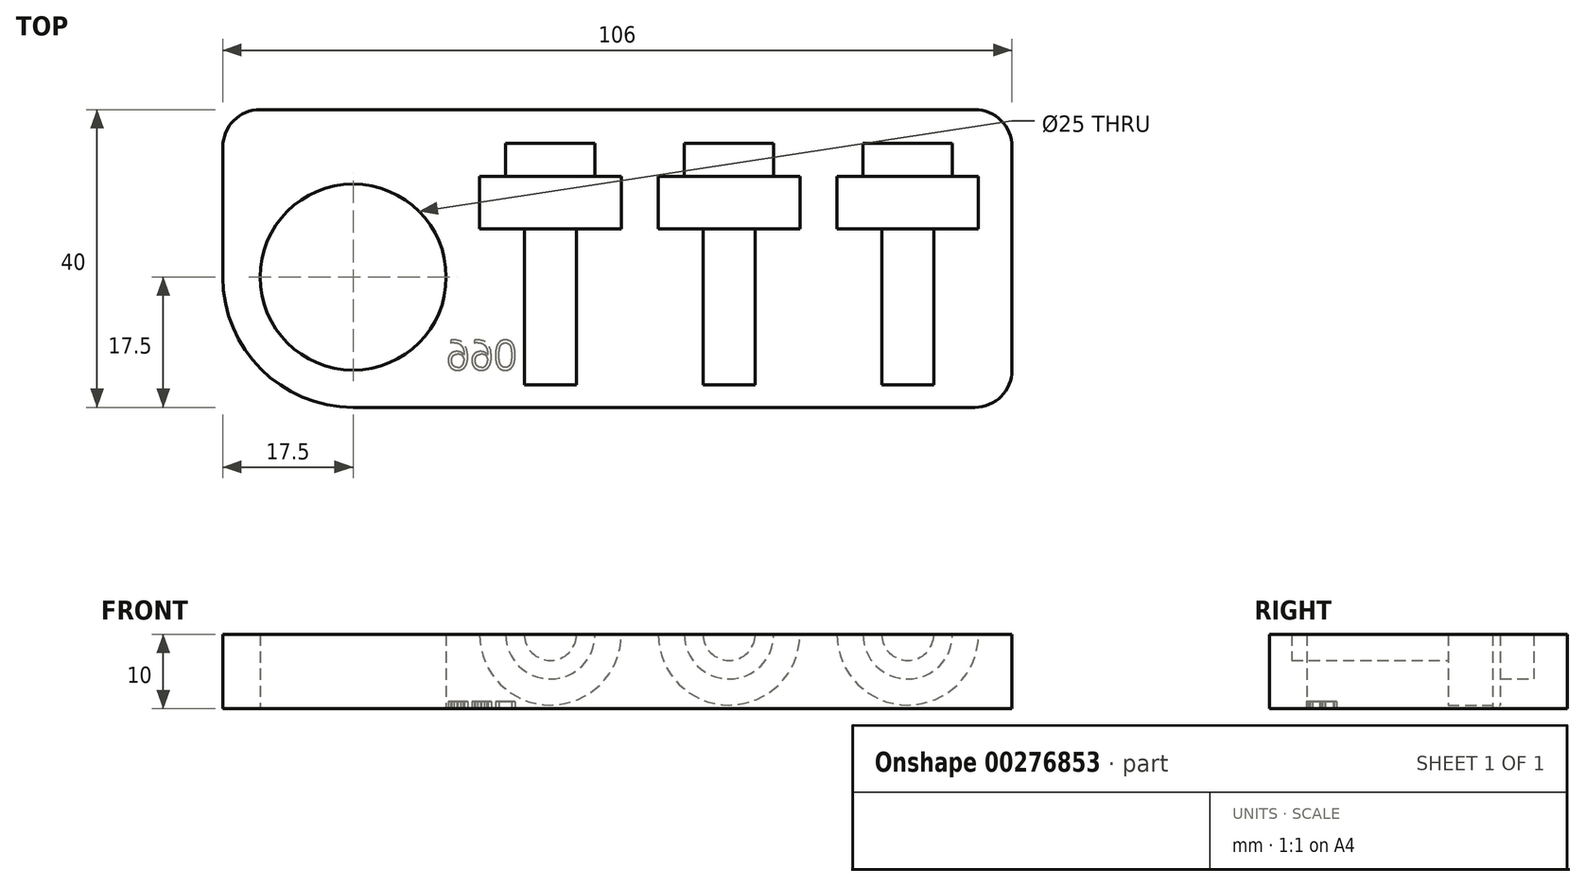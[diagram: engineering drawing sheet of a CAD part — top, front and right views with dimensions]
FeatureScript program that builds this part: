
annotation { "Feature Type Name" : "Feature", "Feature Type Description" : "" }
export const myFeature = defineFeature(function(context is Context, id is Id, definition is map)
    precondition{}
    {
        {
            var Q0;
            Q0=qCreatedBy(makeId("Top.planeOp"),FACE);
            var sketch = newSketch(context, id + "F0", { "sketchPlane" : qUnion([Q0])});
            skLineSegment(sketch, "E0.bottom", {"start": v(17.5, 0) * mm, "end": v(101, 0) * mm});
            skLineSegment(sketch, "E0.top", {"start": v(5, 40) * mm, "end": v(101, 40) * mm});
            skLineSegment(sketch, "E0.left", {"start": v(0, 17.5) * mm, "end": v(0, 35) * mm});
            skLineSegment(sketch, "E0.right", {"start": v(106, 5) * mm, "end": v(106, 35) * mm});
            skLineSegment(sketch, "E1.bottom", {"start": v(0, 0) * mm, "end": v(17.5, 0) * mm, "construction": true});
            skLineSegment(sketch, "E1.top", {"start": v(0, 17.5) * mm, "end": v(17.5, 17.5) * mm, "construction": true});
            skLineSegment(sketch, "E1.left", {"start": v(0, 0) * mm, "end": v(0, 17.5) * mm, "construction": true});
            skLineSegment(sketch, "E1.right", {"start": v(17.5, 0) * mm, "end": v(17.5, 17.5) * mm, "construction": true});
            skCircle(sketch, "E2", {"center": v(17.5, 17.5) * mm, "radius": 12.5 * mm});
            skPoint(sketch, "E3.visualSharp", {"position": v(0, 0) * mm});
            skArc(sketch, "E3.filletArc", {"start": v(0, 17.5) * mm, "mid": v(5.13, 5.13) * mm, "end": v(17.5, 0) * mm});
            skPoint(sketch, "E4.visualSharp", {"position": v(0, 40) * mm});
            skArc(sketch, "E4.filletArc", {"start": v(5, 40) * mm, "mid": v(1.46, 38.54) * mm, "end": v(0, 35) * mm});
            skPoint(sketch, "E5.visualSharp", {"position": v(106, 40) * mm});
            skArc(sketch, "E5.filletArc", {"start": v(106, 35) * mm, "mid": v(104.54, 38.54) * mm, "end": v(101, 40) * mm});
            skPoint(sketch, "E6.visualSharp", {"position": v(106, 0) * mm});
            skArc(sketch, "E6.filletArc", {"start": v(101, 0) * mm, "mid": v(104.54, 1.46) * mm, "end": v(106, 5) * mm});
            skSolve(sketch);
        }
        {
            var Q0;
            Q0=makeQuery(id+"F0.imprint","IMPRINT",FACE,{"disambiguationData":[TD([[makeQuery(id+"F0.imprint","IMPRINT",EDGE,{"derivedFrom":sQuery(id+"F0.wireOp",EDGE,"E0.bottom")}),1.0]])]});
            extrude(context, id + "F1", {"entities" : qUnion([Q0]), "depth" : 10 * mm});
        }
        {
            var Q0;
            Q0=makeQuery(id+"F1.opExtrude","CAP_FACE",FACE,{"disambiguationData":[OSD([sQuery(id+"F0.wireOp",EDGE,"E0.bottom"),sQuery(id+"F0.wireOp",EDGE,"E0.top"),sQuery(id+"F0.wireOp",EDGE,"E0.right"),sQuery(id+"F0.wireOp",EDGE,"E2"),sQuery(id+"F0.wireOp",EDGE,"E3.filletArc"),sQuery(id+"F0.wireOp",EDGE,"E4.filletArc"),sQuery(id+"F0.wireOp",EDGE,"E5.filletArc"),sQuery(id+"F0.wireOp",EDGE,"E6.filletArc")])],"isStart":false});
            var sketch = newSketch(context, id + "F2", { "sketchPlane" : qUnion([Q0])});
            skLineSegment(sketch, "E7.bottom", {"start": v(0, 0) * mm, "end": v(44, 0) * mm, "construction": true});
            skLineSegment(sketch, "E7.top", {"start": v(0, 3) * mm, "end": v(44, 3) * mm, "construction": true});
            skLineSegment(sketch, "E7.left", {"start": v(0, 0) * mm, "end": v(0, 3) * mm, "construction": true});
            skLineSegment(sketch, "E7.right", {"start": v(44, 0) * mm, "end": v(44, 3) * mm, "construction": true});
            skLineSegment(sketch, "E8", {"start": v(44, 3) * mm, "end": v(68, 3) * mm, "construction": true});
            skLineSegment(sketch, "E9", {"start": v(68, 3) * mm, "end": v(92, 3) * mm, "construction": true});
            skLineSegment(sketch, "E10", {"start": v(92, 3) * mm, "end": v(116, 3) * mm, "construction": true});
            skLineSegment(sketch, "E11.bottom", {"start": v(44, 3) * mm, "end": v(47.5, 3) * mm});
            skLineSegment(sketch, "E11.left", {"start": v(44, 3) * mm, "end": v(44, 24) * mm});
            skLineSegment(sketch, "E11.right", {"start": v(47.5, 3) * mm, "end": v(47.5, 24) * mm});
            skLineSegment(sketch, "E12.bottom", {"start": v(68, 3) * mm, "end": v(71.5, 3) * mm});
            skLineSegment(sketch, "E12.left", {"start": v(68, 3) * mm, "end": v(68, 24) * mm});
            skLineSegment(sketch, "E12.right", {"start": v(71.5, 3) * mm, "end": v(71.5, 24) * mm});
            skLineSegment(sketch, "E13.bottom", {"start": v(92, 3) * mm, "end": v(95.5, 3) * mm});
            skLineSegment(sketch, "E13.left", {"start": v(92, 3) * mm, "end": v(92, 24) * mm});
            skLineSegment(sketch, "E13.right", {"start": v(95.5, 3) * mm, "end": v(95.5, 24) * mm});
            skLineSegment(sketch, "E14.bottom", {"start": v(116, 3) * mm, "end": v(119.5, 3) * mm});
            skLineSegment(sketch, "E14.left", {"start": v(116, 3) * mm, "end": v(116, 24) * mm});
            skLineSegment(sketch, "E14.right", {"start": v(119.5, 3) * mm, "end": v(119.5, 24) * mm});
            skLineSegment(sketch, "E15.bottom", {"start": v(47.5, 24) * mm, "end": v(53.5, 24) * mm});
            skLineSegment(sketch, "E15.top", {"start": v(50, 31) * mm, "end": v(53.5, 31) * mm});
            skLineSegment(sketch, "E15.left", {"start": v(44, 24) * mm, "end": v(44, 31) * mm});
            skLineSegment(sketch, "E15.right", {"start": v(53.5, 24) * mm, "end": v(53.5, 31) * mm});
            skLineSegment(sketch, "E16.bottom", {"start": v(71.5, 24) * mm, "end": v(77.5, 24) * mm});
            skLineSegment(sketch, "E16.top", {"start": v(74, 31) * mm, "end": v(77.5, 31) * mm});
            skLineSegment(sketch, "E16.left", {"start": v(68, 24) * mm, "end": v(68, 31) * mm});
            skLineSegment(sketch, "E16.right", {"start": v(77.5, 24) * mm, "end": v(77.5, 31) * mm});
            skLineSegment(sketch, "E17.bottom", {"start": v(95.5, 24) * mm, "end": v(101.5, 24) * mm});
            skLineSegment(sketch, "E17.top", {"start": v(98, 31) * mm, "end": v(101.5, 31) * mm});
            skLineSegment(sketch, "E17.left", {"start": v(92, 24) * mm, "end": v(92, 31) * mm});
            skLineSegment(sketch, "E17.right", {"start": v(101.5, 24) * mm, "end": v(101.5, 31) * mm});
            skLineSegment(sketch, "E18.bottom", {"start": v(119.5, 24) * mm, "end": v(125.5, 24) * mm});
            skLineSegment(sketch, "E18.top", {"start": v(122, 31) * mm, "end": v(125.5, 31) * mm});
            skLineSegment(sketch, "E18.left", {"start": v(116, 24) * mm, "end": v(116, 31) * mm});
            skLineSegment(sketch, "E18.right", {"start": v(125.5, 24) * mm, "end": v(125.5, 31) * mm});
            skLineSegment(sketch, "E19.top", {"start": v(44, 35.5) * mm, "end": v(50, 35.5) * mm});
            skLineSegment(sketch, "E19.left", {"start": v(44, 31) * mm, "end": v(44, 35.5) * mm});
            skLineSegment(sketch, "E19.right", {"start": v(50, 31) * mm, "end": v(50, 35.5) * mm});
            skLineSegment(sketch, "E20.top", {"start": v(68, 35.5) * mm, "end": v(74, 35.5) * mm});
            skLineSegment(sketch, "E20.left", {"start": v(68, 31) * mm, "end": v(68, 35.5) * mm});
            skLineSegment(sketch, "E20.right", {"start": v(74, 31) * mm, "end": v(74, 35.5) * mm});
            skLineSegment(sketch, "E21.top", {"start": v(92, 35.5) * mm, "end": v(98, 35.5) * mm});
            skLineSegment(sketch, "E21.left", {"start": v(92, 31) * mm, "end": v(92, 35.5) * mm});
            skLineSegment(sketch, "E21.right", {"start": v(98, 31) * mm, "end": v(98, 35.5) * mm});
            skLineSegment(sketch, "E22.top", {"start": v(116, 35.5) * mm, "end": v(122, 35.5) * mm});
            skLineSegment(sketch, "E22.left", {"start": v(116, 31) * mm, "end": v(116, 35.5) * mm});
            skLineSegment(sketch, "E22.right", {"start": v(122, 31) * mm, "end": v(122, 35.5) * mm});
            skSolve(sketch);
        }
        {
            var Q0;
            Q0=makeQuery(id+"F2.imprint","IMPRINT",FACE,{"disambiguationData":[TD([[makeQuery(id+"F2.imprint","IMPRINT",EDGE,{"derivedFrom":sQuery(id+"F2.wireOp",EDGE,"E11.bottom")}),1.0]])]});
            var Q1;
            Q1=sQuery(id+"F2.wireOp",EDGE,"E11.left");
            revolve(context, id + "F3", {"operationType" : NewBodyOperationType.REMOVE, "entities" : qUnion([Q0]), "axis" : qUnion([Q1]), "revolveType" : RevolveType.FULL, "oppositeDirection" : true});
        }
        {
            var Q0;
            Q0=makeQuery(id+"F2.imprint","IMPRINT",FACE,{"disambiguationData":[TD([[makeQuery(id+"F2.imprint","IMPRINT",EDGE,{"derivedFrom":sQuery(id+"F2.wireOp",EDGE,"E12.bottom")}),1.0]])]});
            var Q1;
            Q1=sQuery(id+"F2.wireOp",EDGE,"E12.left");
            revolve(context, id + "F4", {"operationType" : NewBodyOperationType.REMOVE, "entities" : qUnion([Q0]), "axis" : qUnion([Q1]), "revolveType" : RevolveType.FULL, "oppositeDirection" : true});
        }
        {
            var Q0;
            Q0=makeQuery(id+"F2.imprint","IMPRINT",FACE,{"disambiguationData":[TD([[makeQuery(id+"F2.imprint","IMPRINT",EDGE,{"derivedFrom":sQuery(id+"F2.wireOp",EDGE,"E13.bottom")}),1.0]])]});
            var Q1;
            Q1=sQuery(id+"F2.wireOp",EDGE,"E13.left");
            revolve(context, id + "F5", {"operationType" : NewBodyOperationType.REMOVE, "entities" : qUnion([Q0]), "axis" : qUnion([Q1]), "revolveType" : RevolveType.FULL, "oppositeDirection" : true});
        }
        {
            var Q0;
            Q0=makeQuery(id+"F1.opExtrude","CAP_FACE",FACE,{"disambiguationData":[OSD([sQuery(id+"F0.wireOp",EDGE,"E0.bottom"),sQuery(id+"F0.wireOp",EDGE,"E0.top"),sQuery(id+"F0.wireOp",EDGE,"E0.left"),sQuery(id+"F0.wireOp",EDGE,"E0.right"),sQuery(id+"F0.wireOp",EDGE,"E2"),sQuery(id+"F0.wireOp",EDGE,"E3.filletArc"),sQuery(id+"F0.wireOp",EDGE,"E4.filletArc"),sQuery(id+"F0.wireOp",EDGE,"E5.filletArc"),sQuery(id+"F0.wireOp",EDGE,"E6.filletArc")])],"isStart":true});
            var sketch = newSketch(context, id + "F6", { "sketchPlane" : qUnion([Q0])});
            skLineSegment(sketch, "E23.bottom", {"start": v(0, 0) * mm, "end": v(30, 0) * mm, "construction": true});
            skLineSegment(sketch, "E23.top", {"start": v(0, -5) * mm, "end": v(30, -5) * mm, "construction": true});
            skLineSegment(sketch, "E23.left", {"start": v(0, 0) * mm, "end": v(0, -5) * mm, "construction": true});
            skLineSegment(sketch, "E23.right", {"start": v(30, 0) * mm, "end": v(30, -5) * mm, "construction": true});
            skText(sketch, "E24", { "text": "990", "fontName": "OpenSans-Regular.ttf"});
            const initialGuessF6  = {"E24": [0.03, -0.009, 1, 0, 0.004]};
            skSetInitialGuess(sketch, initialGuessF6);
            skSolve(sketch);
        }
        {
            var Q0;
            Q0 = qSketchRegion(id + "F6", true);
            extrude(context, id + "F7", {"entities" : qUnion([Q0]), "operationType" : NewBodyOperationType.REMOVE, "oppositeDirection" : true, "depth" : 1 * mm});
        }
    });
